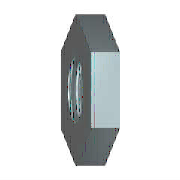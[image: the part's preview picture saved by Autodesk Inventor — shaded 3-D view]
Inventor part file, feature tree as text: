
AUTODESK INVENTOR PART (.ipt)
format: ipt  version: 2019 (Build 230136000, 136)  size: 136,704 bytes
history: native  units: mm (DEFAULTED — no unit token found)
features: other x4, sketch x2, extrude x1, chamfer x1
ambient origin geometry x8: Origin, YZ Plane, XZ Plane, XY Plane, X Axis, Y Axis, Z Axis, Center Point
bodies: Solid1 (feature_tree)
feature tree (8):
  extrude  "Extrusion1"  TaperAngle=0.0deg  [1 undecoded]
  other  "MSC_A1"
  other  "MSC_PT1"
  other  "MSC_PT2"
  other  "MSC_PF1"
  chamfer  "Chamfer1"  [1 undecoded]
  sketch  "Sketch1"  dims[d2=0.0mm]
  sketch  "Sketch2"  dims[d3=3.242mm d4=2.2mm d5=4.0mm d6=2.0mm d7=60.0deg d8=8.0mm d9=20.594885mm d14=0.0mm d15=0.0mm d16=0.0mm d17=0.42mm d18=0.42mm d20=45.0deg d21=0.0mm d23=0.0mm d24=0.0mm d25=0.0mm]
note: 2 required parameter values undecoded (feature->parameter linkage not recoverable at this tier; creation-order binding heuristic only, values carry confidence <= 0.55)
